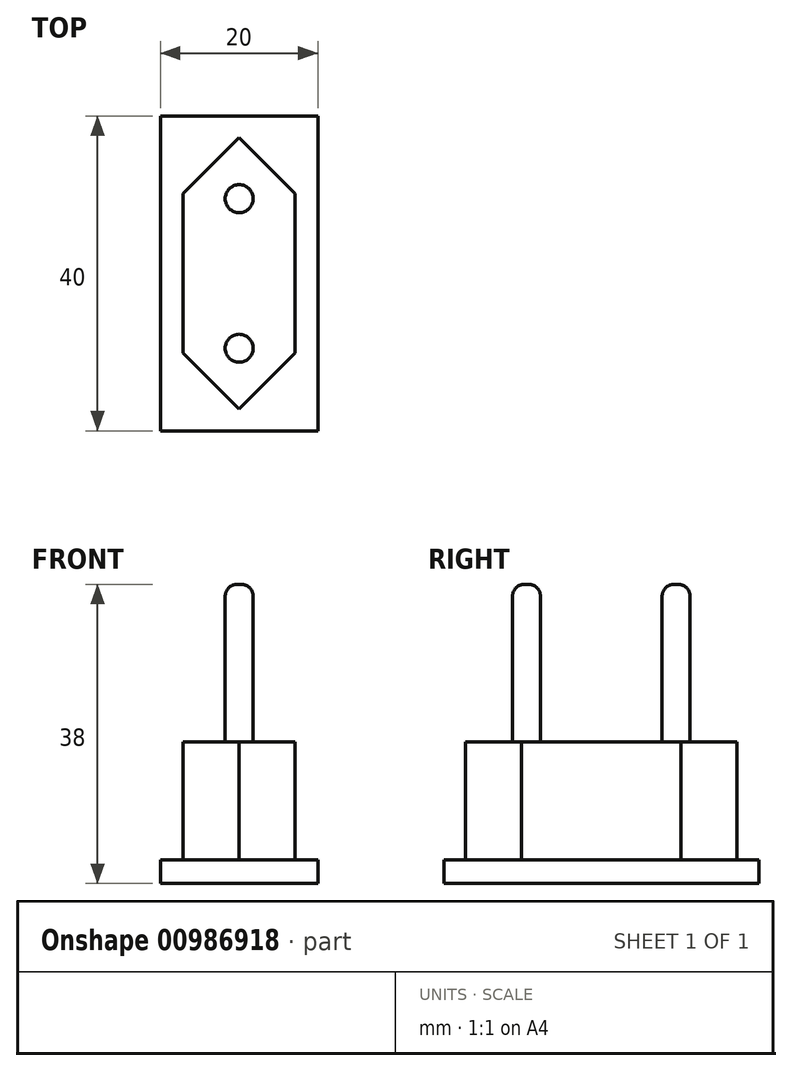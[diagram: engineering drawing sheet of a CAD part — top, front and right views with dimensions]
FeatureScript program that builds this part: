
annotation { "Feature Type Name" : "Feature", "Feature Type Description" : "" }
export const myFeature = defineFeature(function(context is Context, id is Id, definition is map)
    precondition{}
    {
        {
            var Q0;
            Q0=qCreatedBy(makeId("Top.planeOp"),FACE);
            var sketch = newSketch(context, id + "F0", { "sketchPlane" : qUnion([Q0])});
            skLineSegment(sketch, "E0.bottom", {"start": v(-7.12, 10.13) * mm, "end": v(7.13, 10.13) * mm});
            skLineSegment(sketch, "E0.top", {"start": v(-7.12, -10.12) * mm, "end": v(7.13, -10.12) * mm});
            skLineSegment(sketch, "E0.left", {"start": v(-7.12, 10.12) * mm, "end": v(-7.12, -10.13) * mm});
            skLineSegment(sketch, "E0.right", {"start": v(7.13, 10.13) * mm, "end": v(7.13, -10.12) * mm});
            skPoint(sketch, "E0.middle", {"position": v(0, 0) * mm});
            skLineSegment(sketch, "E1", {"start": v(-7.12, 10.12) * mm, "end": v(0, 17.25) * mm});
            skPoint(sketch, "E1.endSnap0", {"position": v(0, 10.13) * mm});
            skLineSegment(sketch, "E2", {"start": v(0, 17.25) * mm, "end": v(7.13, 10.12) * mm});
            skLineSegment(sketch, "E3", {"start": v(-7.12, -10.13) * mm, "end": v(0, -17.25) * mm});
            skLineSegment(sketch, "E4", {"start": v(0, -17.25) * mm, "end": v(7.13, -10.13) * mm});
            skSolve(sketch);
        }
        {
            var Q0;
            Q0=makeQuery(id+"F0.imprint","IMPRINT",FACE,{"disambiguationData":[TD([[makeQuery(id+"F0.imprint","IMPRINT",EDGE,{"derivedFrom":sQuery(id+"F0.wireOp",EDGE,"E0.top")}),-1.0]])]});
            var Q1;
            Q1 = qSketchRegion(id + "F0", true);
            extrude(context, id + "F1", {"entities" : qUnion([Q0, Q1]), "depth" : 18 * mm, "offsetDistance" : 25 * mm});
        }
        {
            var Q0;
            Q0=qCreatedBy(makeId("Top.planeOp"),FACE);
            var sketch = newSketch(context, id + "F2", { "sketchPlane" : qUnion([Q0])});
            skLineSegment(sketch, "E5.bottom", {"start": v(-10, -20) * mm, "end": v(10, -20) * mm});
            skLineSegment(sketch, "E5.top", {"start": v(-10, 20) * mm, "end": v(10, 20) * mm});
            skLineSegment(sketch, "E5.left", {"start": v(-10, -20) * mm, "end": v(-10, 20) * mm});
            skLineSegment(sketch, "E5.right", {"start": v(10, -20) * mm, "end": v(10, 20) * mm});
            skPoint(sketch, "E5.middle", {"position": v(0, 0) * mm});
            skSolve(sketch);
        }
        {
            var Q0;
            Q0 = qSketchRegion(id + "F2", true);
            extrude(context, id + "F3", {"entities" : qUnion([Q0]), "operationType" : NewBodyOperationType.ADD, "depth" : 3 * mm, "offsetDistance" : 25 * mm});
        }
        {
            var Q0;
            Q0=makeQuery(id+"F1.opExtrude","CAP_FACE",FACE,{"disambiguationData":[OSD([sQuery(id+"F0.wireOp",EDGE,"E0.left"),sQuery(id+"F0.wireOp",EDGE,"E0.right"),sQuery(id+"F0.wireOp",EDGE,"E1"),sQuery(id+"F0.wireOp",EDGE,"E2"),sQuery(id+"F0.wireOp",EDGE,"E3"),sQuery(id+"F0.wireOp",EDGE,"E4")])],"isStart":false});
            var sketch = newSketch(context, id + "F4", { "sketchPlane" : qUnion([Q0])});
            skCircle(sketch, "E6", {"center": v(0, 9.5) * mm, "radius": 1.77 * mm});
            skCircle(sketch, "E7.MirrorC", {"center": v(0, -9.5) * mm, "radius": 1.77 * mm});
            skSolve(sketch);
        }
        {
            var Q0;
            Q0 = qSketchRegion(id + "F4", true);
            extrude(context, id + "F5", {"entities" : qUnion([Q0]), "operationType" : NewBodyOperationType.ADD, "depth" : 20 * mm, "offsetDistance" : 25 * mm});
        }
        {
            var Q0;
            Q0=makeQuery(id+"F5.opExtrude","CAP_EDGE",EDGE,{"disambiguationData":[OSD([sQuery(id+"F4.wireOp",EDGE,"E7.MirrorC")])],"isStart":false});
            var Q1;
            Q1=makeQuery(id+"F5.opExtrude","CAP_EDGE",EDGE,{"disambiguationData":[OSD([sQuery(id+"F4.wireOp",EDGE,"E6")])],"isStart":false});
            fillet(context, id + "F6", {"entities" : qUnion([Q0, Q1]), "radius" : 1.5 * mm, "tangentPropagation" : true, "allowEdgeOverflow" : false});
        }
    });
